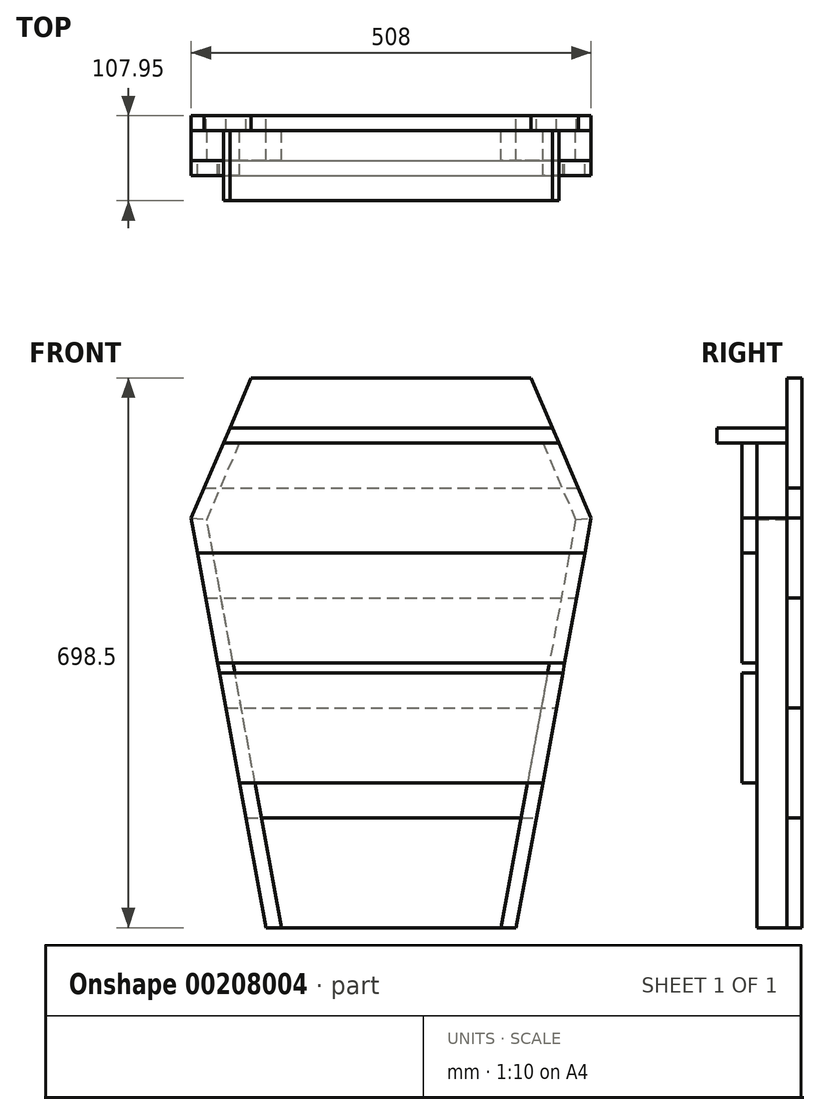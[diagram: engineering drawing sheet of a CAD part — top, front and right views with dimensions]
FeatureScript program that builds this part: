
annotation { "Feature Type Name" : "Feature", "Feature Type Description" : "" }
export const myFeature = defineFeature(function(context is Context, id is Id, definition is map)
    precondition{}
    {
        {
            var Q0;
            Q0=qCreatedBy(makeId("Front.planeOp"),FACE);
            var sketch = newSketch(context, id + "F0", { "sketchPlane" : qUnion([Q0])});
            skLineSegment(sketch, "E0", {"start": v(0, 0) * mm, "end": v(0, -698.5) * mm, "construction": true});
            skLineSegment(sketch, "E1", {"start": v(-177.8, 0) * mm, "end": v(177.8, 0) * mm});
            skLineSegment(sketch, "E2", {"start": v(177.8, 0) * mm, "end": v(254, -177.8) * mm});
            skLineSegment(sketch, "E3", {"start": v(254, -177.8) * mm, "end": v(158.75, -698.5) * mm});
            skLineSegment(sketch, "E4", {"start": v(158.75, -698.5) * mm, "end": v(-158.75, -698.5) * mm});
            skLineSegment(sketch, "E5", {"start": v(-158.75, -698.5) * mm, "end": v(-254, -177.8) * mm});
            skLineSegment(sketch, "E6", {"start": v(-254, -177.8) * mm, "end": v(-177.8, 0) * mm});
            skSolve(sketch);
        }
        {
            var Q0;
            Q0=qCreatedBy(makeId("Front.planeOp"),FACE);
            var sketch = newSketch(context, id + "F1", { "sketchPlane" : qUnion([Q0])});
            skLineSegment(sketch, "E7.0", {"start": v(-158.75, -698.5) * mm, "end": v(-254, -177.8) * mm});
            skLineSegment(sketch, "E8.0", {"start": v(-254, -177.8) * mm, "end": v(-177.8, 0) * mm});
            skLineSegment(sketch, "E8.1", {"start": v(-177.8, 0) * mm, "end": v(177.8, 0) * mm});
            skLineSegment(sketch, "E8.2", {"start": v(177.8, 0) * mm, "end": v(254, -177.8) * mm});
            skLineSegment(sketch, "E8.3", {"start": v(254, -177.8) * mm, "end": v(158.75, -698.5) * mm});
            skLineSegment(sketch, "E9", {"start": v(-237.67, -139.7) * mm, "end": v(237.67, -139.7) * mm});
            skLineSegment(sketch, "E10", {"start": v(-235.41, -279.4) * mm, "end": v(235.41, -279.4) * mm});
            skLineSegment(sketch, "E11", {"start": v(-209.86, -419.1) * mm, "end": v(209.86, -419.1) * mm});
            skLineSegment(sketch, "E12", {"start": v(-184.3, -558.8) * mm, "end": v(184.3, -558.8) * mm});
            skLineSegment(sketch, "E13", {"start": v(-158.75, -698.5) * mm, "end": v(158.75, -698.5) * mm});
            skSolve(sketch);
        }
        {
            var Q0;
            {var subQ0=sQuery(id+"F1.wireOp",EDGE,"E11");Q0=makeQuery(id+"F1.imprint","IMPRINT",FACE,{"disambiguationData":[TD([[makeQuery(id+"F1.imprint","IMPRINT",EDGE,{"derivedFrom":subQ0}),-1.0]])]});}
            var Q1;
            {var subQ7=sQuery(id+"F1.wireOp",EDGE,"E9");Q1=makeQuery(id+"F1.imprint","IMPRINT",FACE,{"disambiguationData":[TD([[makeQuery(id+"F1.imprint","IMPRINT",EDGE,{"derivedFrom":subQ7}),-1.0]])]});}
            extrude(context, id + "F2", {"entities" : qUnion([Q0, Q1]), "depth" : 19.05 * mm});
        }
        {
            var Q0;
            {var subQ0=sQuery(id+"F1.wireOp",EDGE,"E12");Q0=makeQuery(id+"F1.imprint","IMPRINT",FACE,{"disambiguationData":[TD([[makeQuery(id+"F1.imprint","IMPRINT",EDGE,{"derivedFrom":subQ0}),-1.0]])]});}
            var Q1;
            {var subQ0=sQuery(id+"F1.wireOp",EDGE,"E10");Q1=makeQuery(id+"F1.imprint","IMPRINT",FACE,{"disambiguationData":[TD([[makeQuery(id+"F1.imprint","IMPRINT",EDGE,{"derivedFrom":subQ0}),-1.0]])]});}
            var Q2;
            {var subQ0=sQuery(id+"F1.wireOp",EDGE,"E8.1");Q2=makeQuery(id+"F1.imprint","IMPRINT",FACE,{"disambiguationData":[TD([[makeQuery(id+"F1.imprint","IMPRINT",EDGE,{"derivedFrom":subQ0}),-1.0]])]});}
            extrude(context, id + "F3", {"entities" : qUnion([Q0, Q1, Q2]), "depth" : 19.05 * mm});
        }
        {
            var Q0;
            Q0=makeQuery(id+"F3.opExtrude","CAP_FACE",FACE,{"disambiguationData":[OSD([sQuery(id+"F1.wireOp",EDGE,"E8.0"),sQuery(id+"F1.wireOp",EDGE,"E8.1"),sQuery(id+"F1.wireOp",EDGE,"E8.2"),sQuery(id+"F1.wireOp",EDGE,"E9")])],"isStart":false});
            var sketch = newSketch(context, id + "F4", { "sketchPlane" : qUnion([Q0])});
            skLineSegment(sketch, "E14.0", {"start": v(-158.75, -698.5) * mm, "end": v(-254, -177.8) * mm});
            skLineSegment(sketch, "E14.1", {"start": v(-254, -177.8) * mm, "end": v(-205.01, -63.5) * mm});
            skLineSegment(sketch, "E14.3", {"start": v(205.01, -63.5) * mm, "end": v(254, -177.8) * mm});
            skLineSegment(sketch, "E14.4", {"start": v(254, -177.8) * mm, "end": v(158.75, -698.5) * mm});
            skLineSegment(sketch, "E14.9", {"start": v(-158.75, -698.5) * mm, "end": v(-139.38, -698.5) * mm});
            skLineSegment(sketch, "E15.0", {"start": v(-139.38, -698.5) * mm, "end": v(-234.23, -180.02) * mm});
            skLineSegment(sketch, "E16.0", {"start": v(-234.23, -180.02) * mm, "end": v(-192.45, -82.55) * mm});
            skLineSegment(sketch, "E17.0", {"start": v(-213.18, -82.55) * mm, "end": v(213.18, -82.55) * mm});
            skLineSegment(sketch, "E18.0", {"start": v(192.45, -82.55) * mm, "end": v(234.23, -180.02) * mm});
            skLineSegment(sketch, "E19.0", {"start": v(234.23, -180.02) * mm, "end": v(139.38, -698.5) * mm});
            skLineSegment(sketch, "E20", {"start": v(234.23, -180.02) * mm, "end": v(254, -177.8) * mm});
            skLineSegment(sketch, "E21", {"start": v(-254, -177.8) * mm, "end": v(-234.23, -180.02) * mm});
            skLineSegment(sketch, "E22.trimOffspring", {"start": v(139.38, -698.5) * mm, "end": v(158.75, -698.5) * mm});
            skLineSegment(sketch, "E23", {"start": v(-205.01, -63.5) * mm, "end": v(205.01, -63.5) * mm});
            skPoint(sketch, "E24.orphan", {"position": v(-177.8, 0) * mm});
            skPoint(sketch, "E25.orphan", {"position": v(177.8, 0) * mm});
            skSolve(sketch);
        }
        {
            var Q0;
            {var subQ0=sQuery(id+"F4.wireOp",EDGE,"E14.1");var subQ1=makeQuery(id+"F3.opExtrude","CAP_EDGE",EDGE,{"disambiguationData":[OSD([sQuery(id+"F1.wireOp",EDGE,"E9")])],"isStart":false});var subQ2=makeQuery(id+"F4.imprint","INTERSECT",VERTEX,{"derivedFrom":[subQ1,subQ0]});Q0=makeQuery(id+"F4.imprint","IMPRINT",FACE,{"disambiguationData":[TD([[makeQuery(id+"F4.imprint","IMPRINT",EDGE,{"disambiguationData":[TD([[subQ2,-1.0]])],"derivedFrom":subQ0}),-1.0]])]});}
            var Q1;
            {var subQ3=sQuery(id+"F4.wireOp",EDGE,"E21");Q1=makeQuery(id+"F4.imprint","IMPRINT",FACE,{"disambiguationData":[TD([[makeQuery(id+"F4.imprint","IMPRINT",EDGE,{"derivedFrom":subQ3}),1.0]])]});}
            var Q2;
            {var subQ0=sQuery(id+"F4.wireOp",EDGE,"E14.3");var subQ1=makeQuery(id+"F3.opExtrude","CAP_EDGE",EDGE,{"disambiguationData":[OSD([sQuery(id+"F1.wireOp",EDGE,"E9")])],"isStart":false});var subQ2=makeQuery(id+"F4.imprint","INTERSECT",VERTEX,{"derivedFrom":[subQ1,subQ0]});Q2=makeQuery(id+"F4.imprint","IMPRINT",FACE,{"disambiguationData":[TD([[makeQuery(id+"F4.imprint","IMPRINT",EDGE,{"disambiguationData":[TD([[subQ2,1.0]])],"derivedFrom":subQ0}),-1.0]])]});}
            var Q3;
            {var subQ3=sQuery(id+"F4.wireOp",EDGE,"E20");Q3=makeQuery(id+"F4.imprint","IMPRINT",FACE,{"disambiguationData":[TD([[makeQuery(id+"F4.imprint","IMPRINT",EDGE,{"derivedFrom":subQ3}),1.0]])]});}
            extrude(context, id + "F5", {"entities" : qUnion([Q0, Q1, Q2, Q3]), "depth" : 38.1 * mm});
        }
        {
            var Q0;
            {var subQ0=sQuery(id+"F4.wireOp",EDGE,"E14.2");Q0=makeQuery(id+"F4.imprint","IMPRINT",FACE,{"disambiguationData":[TD([[makeQuery(id+"F4.imprint","IMPRINT",EDGE,{"derivedFrom":subQ0}),-1.0]])]});}
            var Q1;
            Q1=makeQuery(id+"F4.imprint","IMPRINT",FACE,{"disambiguationData":[TD([[makeQuery(id+"F4.imprint","IMPRINT",EDGE,{"derivedFrom":sQuery(id+"F4.wireOp",EDGE,"E14.0")}),-1.0]])]});
            var Q2;
            Q2=makeQuery(id+"F4.imprint","IMPRINT",FACE,{"disambiguationData":[TD([[makeQuery(id+"F4.imprint","IMPRINT",EDGE,{"derivedFrom":sQuery(id+"F4.wireOp",EDGE,"E14.4")}),-1.0]])]});
            extrude(context, id + "F6", {"entities" : qUnion([Q0, Q1, Q2]), "depth" : 38.1 * mm});
        }
        {
            var Q0;
            {var subQ4=sQuery(id+"F4.wireOp",EDGE,"E23");Q0=makeQuery(id+"F4.imprint","IMPRINT",FACE,{"disambiguationData":[TD([[makeQuery(id+"F4.imprint","IMPRINT",EDGE,{"derivedFrom":subQ4}),-1.0]])]});}
            extrude(context, id + "F7", {"entities" : qUnion([Q0]), "depth" : 88.9 * mm});
        }
        {
            var Q0;
            Q0=makeQuery(id+"F5.opExtrude","CAP_FACE",FACE,{"disambiguationData":[OSD([sQuery(id+"F4.wireOp",EDGE,"E14.3"),sQuery(id+"F4.wireOp",EDGE,"E17.0"),sQuery(id+"F4.wireOp",EDGE,"E18.0"),sQuery(id+"F4.wireOp",EDGE,"E20")])],"isStart":false});
            var sketch = newSketch(context, id + "F8", { "sketchPlane" : qUnion([Q0])});
            skLineSegment(sketch, "E26.0", {"start": v(-213.18, -82.55) * mm, "end": v(213.18, -82.55) * mm});
            skLineSegment(sketch, "E27", {"start": v(-245.87, -222.25) * mm, "end": v(245.87, -222.25) * mm});
            skLineSegment(sketch, "E28", {"start": v(-220.31, -361.95) * mm, "end": v(220.31, -361.95) * mm});
            skLineSegment(sketch, "E29", {"start": v(-218, -374.65) * mm, "end": v(218, -374.65) * mm});
            skLineSegment(sketch, "E30", {"start": v(-192.44, -514.35) * mm, "end": v(192.44, -514.35) * mm});
            skLineSegment(sketch, "E31.0", {"start": v(-254, -177.8) * mm, "end": v(-213.18, -82.55) * mm});
            skLineSegment(sketch, "E31.1", {"start": v(-158.75, -698.5) * mm, "end": v(-254, -177.8) * mm});
            skLineSegment(sketch, "E31.2", {"start": v(213.18, -82.55) * mm, "end": v(254, -177.8) * mm});
            skLineSegment(sketch, "E31.3", {"start": v(254, -177.8) * mm, "end": v(158.75, -698.5) * mm});
            skSolve(sketch);
        }
        {
            var Q0;
            {var subQ1=sQuery(id+"F8.wireOp",EDGE,"E27");Q0=makeQuery(id+"F8.imprint","IMPRINT",FACE,{"disambiguationData":[TD([[makeQuery(id+"F8.imprint","IMPRINT",EDGE,{"derivedFrom":subQ1}),1.0]])]});}
            var Q1;
            {var subQ0=sQuery(id+"F8.wireOp",EDGE,"E29");Q1=makeQuery(id+"F8.imprint","IMPRINT",FACE,{"disambiguationData":[TD([[makeQuery(id+"F8.imprint","IMPRINT",EDGE,{"derivedFrom":subQ0}),-1.0]])]});}
            var Q2;
            {var subQ0=sQuery(id+"F8.wireOp",EDGE,"E31.2");Q2=makeQuery(id+"F8.imprint","IMPRINT",FACE,{"disambiguationData":[TD([[makeQuery(id+"F8.imprint","IMPRINT",EDGE,{"derivedFrom":subQ0}),-1.0]])]});}
            extrude(context, id + "F9", {"entities" : qUnion([Q0, Q1, Q2]), "depth" : 19.05 * mm});
        }
        {
            var Q0;
            {var subQ0=sQuery(id+"F8.wireOp",EDGE,"E27");Q0=makeQuery(id+"F8.imprint","IMPRINT",FACE,{"disambiguationData":[TD([[makeQuery(id+"F8.imprint","IMPRINT",EDGE,{"derivedFrom":subQ0}),-1.0]])]});}
            extrude(context, id + "F10", {"entities" : qUnion([Q0]), "depth" : 19.05 * mm});
        }
    });
